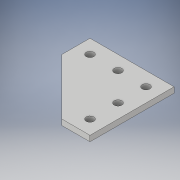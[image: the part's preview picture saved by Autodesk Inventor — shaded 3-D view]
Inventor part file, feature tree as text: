
AUTODESK INVENTOR PART (.ipt)
format: ipt  version: 2019 (Build 230136000, 136)  size: 110,592 bytes
history: native  units: in
note: dims shown in document units (in); Inventor stores cm internally (conversion verified against a paired STEP export)
features: extrude x1, sketch x1
ambient origin geometry x8: Origin, YZ Plane, XZ Plane, XY Plane, X Axis, Y Axis, Z Axis, Center Point
bodies: Solid1 (feature_tree)
feature tree (2):
  extrude  "Extrusion1"  Depth=2.3622in
  sketch  "Sketch1"  dims[d0=2.3622in d1=2.3622in d4=0.2165in d5=0.2165in d6=0.2165in d7=0.2165in d8=0.2165in d9=0.1575in d10=0.0in]
